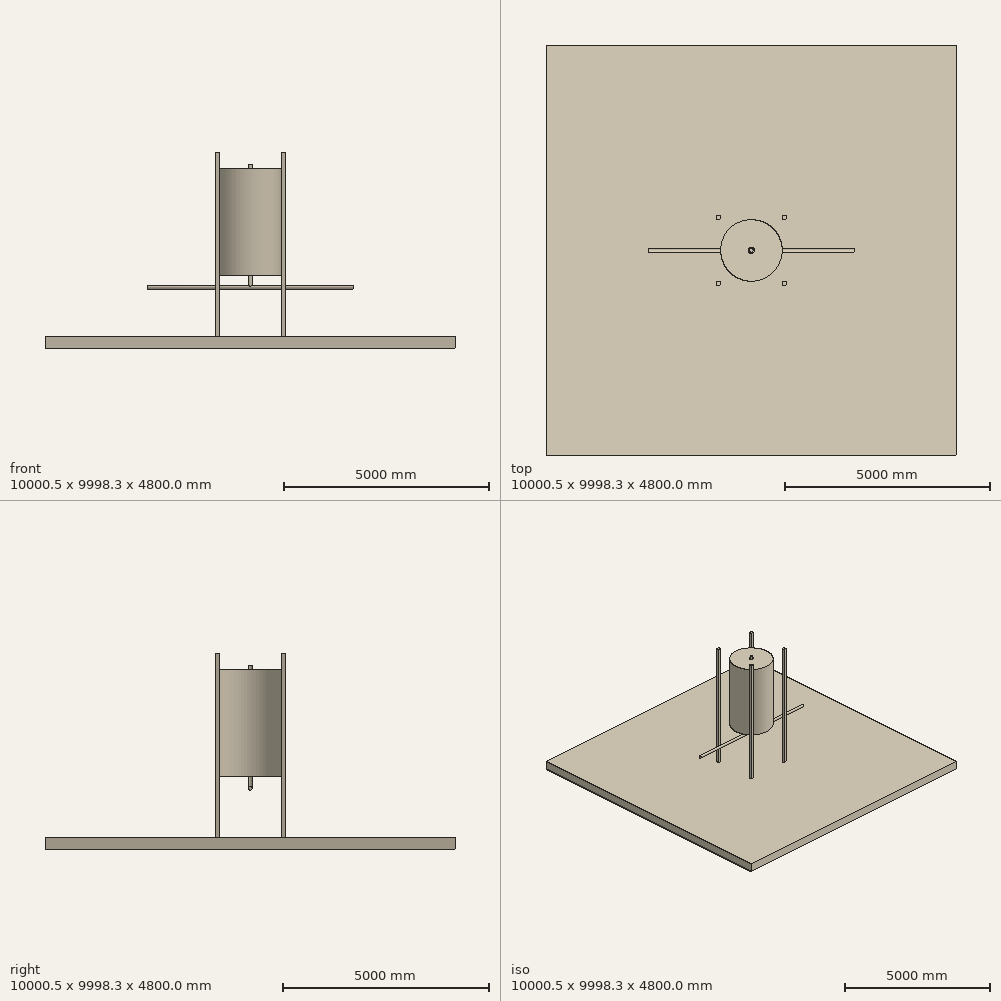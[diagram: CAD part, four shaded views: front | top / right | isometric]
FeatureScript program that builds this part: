
annotation { "Feature Type Name" : "Feature", "Feature Type Description" : "" }
export const myFeature = defineFeature(function(context is Context, id is Id, definition is map)
    precondition{}
    {
        {
            var Q0;
            Q0=qCreatedBy(makeId("Top.planeOp"),FACE);
            var sketch = newSketch(context, id + "F0", { "sketchPlane" : qUnion([Q0])});
            skLineSegment(sketch, "E0.bottom", {"start": v(-5000.27, -4999.16) * mm, "end": v(5000.27, -4999.16) * mm});
            skLineSegment(sketch, "E0.top", {"start": v(-5000.27, 4999.16) * mm, "end": v(5000.27, 4999.16) * mm});
            skLineSegment(sketch, "E0.left", {"start": v(-5000.27, -4999.16) * mm, "end": v(-5000.27, 4999.16) * mm});
            skLineSegment(sketch, "E0.right", {"start": v(5000.27, -4999.16) * mm, "end": v(5000.27, 4999.16) * mm});
            skPoint(sketch, "E0.middle", {"position": v(0, 0) * mm});
            skSolve(sketch);
        }
        {
            var Q0;
            Q0=makeQuery(id+"F0.imprint","IMPRINT",FACE,{"disambiguationData":[TD([[makeQuery(id+"F0.imprint","IMPRINT",EDGE,{"derivedFrom":sQuery(id+"F0.wireOp",EDGE,"E0.bottom")}),1.0]])]});
            extrude(context, id + "F1", {"entities" : qUnion([Q0]), "oppositeDirection" : true, "depth" : 300 * mm, "offsetDistance" : 25 * mm});
        }
        {
            var Q0;
            Q0=qCreatedBy(makeId("Right.planeOp"),FACE);
            var sketch = newSketch(context, id + "F2", { "sketchPlane" : qUnion([Q0])});
            skLineSegment(sketch, "E1", {"start": v(0, 0) * mm, "end": v(0, 1200) * mm});
            skCircle(sketch, "E2", {"center": v(0, 1200) * mm, "radius": 50 * mm});
            skSolve(sketch);
        }
        {
            var Q0;
            Q0=makeQuery(id+"F2.imprint","IMPRINT",FACE,{"disambiguationData":[TD([[makeQuery(id+"F2.imprint","IMPRINT",EDGE,{"derivedFrom":sQuery(id+"F2.wireOp",EDGE,"E2")}),1.0]])]});
            extrude(context, id + "F3", {"entities" : qUnion([Q0]), "endBound" : BoundingType.SYMMETRIC, "depth" : 5000 * mm, "offsetDistance" : 25 * mm});
        }
        {
            var Q0;
            Q0=qCreatedBy(makeId("Top.planeOp"),FACE);
            var sketch = newSketch(context, id + "F4", { "sketchPlane" : qUnion([Q0])});
            skCircle(sketch, "E3", {"center": v(0, 0) * mm, "radius": 750 * mm});
            skSolve(sketch);
        }
        {
            var Q0;
            Q0=makeQuery(id+"F4.imprint","IMPRINT",FACE,{"disambiguationData":[TD([[makeQuery(id+"F4.imprint","IMPRINT",EDGE,{"derivedFrom":sQuery(id+"F4.wireOp",EDGE,"E3")}),1.0]])]});
            extrude(context, id + "F5", {"entities" : qUnion([Q0]), "depth" : 4100 * mm, "offsetDistance" : 25 * mm, "hasSecondDirection" : true, "secondDirectionOppositeDirection" : false, "secondDirectionDepth" : 1500 * mm});
        }
        {
            var Q0;
            Q0=qCreatedBy(makeId("Top.planeOp"),FACE);
            var sketch = newSketch(context, id + "F6", { "sketchPlane" : qUnion([Q0])});
            skPoint(sketch, "E4.middle", {"position": v(0, 0) * mm});
            skLineSegment(sketch, "E5.bottom", {"start": v(-750, 750) * mm, "end": v(-850, 750) * mm});
            skLineSegment(sketch, "E5.top", {"start": v(-750, 850) * mm, "end": v(-850, 850) * mm});
            skLineSegment(sketch, "E5.left", {"start": v(-750, 750) * mm, "end": v(-750, 850) * mm});
            skLineSegment(sketch, "E5.right", {"start": v(-850, 750) * mm, "end": v(-850, 850) * mm});
            skPoint(sketch, "E5.middle", {"position": v(-800, 800) * mm});
            skLineSegment(sketch, "E6.bottom", {"start": v(850, 750) * mm, "end": v(750, 750) * mm});
            skLineSegment(sketch, "E6.top", {"start": v(850, 850) * mm, "end": v(750, 850) * mm});
            skLineSegment(sketch, "E6.left", {"start": v(850, 750) * mm, "end": v(850, 850) * mm});
            skLineSegment(sketch, "E6.right", {"start": v(750, 750) * mm, "end": v(750, 850) * mm});
            skPoint(sketch, "E6.middle", {"position": v(800, 800) * mm});
            skLineSegment(sketch, "E7.bottom", {"start": v(850, -850) * mm, "end": v(750, -850) * mm});
            skLineSegment(sketch, "E7.top", {"start": v(850, -750) * mm, "end": v(750, -750) * mm});
            skLineSegment(sketch, "E7.left", {"start": v(850, -850) * mm, "end": v(850, -750) * mm});
            skLineSegment(sketch, "E7.right", {"start": v(750, -850) * mm, "end": v(750, -750) * mm});
            skPoint(sketch, "E7.middle", {"position": v(800, -800) * mm});
            skLineSegment(sketch, "E8.bottom", {"start": v(-750, -850) * mm, "end": v(-850, -850) * mm});
            skLineSegment(sketch, "E8.top", {"start": v(-750, -750) * mm, "end": v(-850, -750) * mm});
            skLineSegment(sketch, "E8.left", {"start": v(-750, -850) * mm, "end": v(-750, -750) * mm});
            skLineSegment(sketch, "E8.right", {"start": v(-850, -850) * mm, "end": v(-850, -750) * mm});
            skPoint(sketch, "E8.middle", {"position": v(-800, -800) * mm});
            skSolve(sketch);
        }
        {
            var Q0;
            Q0=makeQuery(id+"F6.imprint","IMPRINT",FACE,{"disambiguationData":[TD([[makeQuery(id+"F6.imprint","IMPRINT",EDGE,{"derivedFrom":sQuery(id+"F6.wireOp",EDGE,"E6.bottom")}),-1.0]])]});
            var Q1;
            Q1=makeQuery(id+"F6.imprint","IMPRINT",FACE,{"disambiguationData":[TD([[makeQuery(id+"F6.imprint","IMPRINT",EDGE,{"derivedFrom":sQuery(id+"F6.wireOp",EDGE,"E7.bottom")}),-1.0]])]});
            var Q2;
            Q2=makeQuery(id+"F6.imprint","IMPRINT",FACE,{"disambiguationData":[TD([[makeQuery(id+"F6.imprint","IMPRINT",EDGE,{"derivedFrom":sQuery(id+"F6.wireOp",EDGE,"E8.bottom")}),-1.0]])]});
            var Q3;
            Q3=makeQuery(id+"F6.imprint","IMPRINT",FACE,{"disambiguationData":[TD([[makeQuery(id+"F6.imprint","IMPRINT",EDGE,{"derivedFrom":sQuery(id+"F6.wireOp",EDGE,"E5.bottom")}),-1.0]])]});
            extrude(context, id + "F7", {"entities" : qUnion([Q0, Q1, Q2, Q3]), "depth" : 4500 * mm, "offsetDistance" : 25 * mm});
        }
        {
            var Q0;
            Q0=makeQuery(id+"F5.opExtrude","CAP_FACE",FACE,{"disambiguationData":[OSD([sQuery(id+"F4.wireOp",EDGE,"E3")])],"isStart":false});
            var sketch = newSketch(context, id + "F8", { "sketchPlane" : qUnion([Q0])});
            skCircle(sketch, "E9", {"center": v(0, 0) * mm, "radius": 75 * mm});
            skCircle(sketch, "E10", {"center": v(0, 0) * mm, "radius": 50 * mm});
            skSolve(sketch);
        }
        {
            var Q0;
            Q0=sQuery(id+"F8.wireOp",VERTEX,"E9.center");
            var Q1;
            Q1=makeQuery(id+"F5.opExtrude","SWEPT_BODY",BODY,{"disambiguationData":[OSD([sQuery(id+"F4.wireOp",EDGE,"E3")])]});
            hole(context, id + "F9", {"style" : HoleStyle.SIMPLE, "endStyle" : HoleEndStyle.THROUGH, "holeDiameter" : 150 * mm, "majorDiameter" : 5 * mm, "isTappedThrough" : true, "tappedDepth" : 12 * mm, "tapClearance" : 3, "startFromSketch" : true, "locations" : qUnion([Q0]), "scope" : qUnion([Q1])});
        }
        {
            var Q0;
            Q0=makeQuery(id+"F8.imprint","IMPRINT",FACE,{"disambiguationData":[TD([[makeQuery(id+"F8.imprint","IMPRINT",EDGE,{"derivedFrom":sQuery(id+"F8.wireOp",EDGE,"E10")}),1.0]])]});
            extrude(context, id + "F10", {"entities" : qUnion([Q0]), "operationType" : NewBodyOperationType.ADD, "oppositeDirection" : true, "depth" : 2900 * mm, "offsetDistance" : 25 * mm, "hasSecondDirection" : true, "secondDirectionOppositeDirection" : false, "secondDirectionDepth" : 100 * mm});
        }
    });
